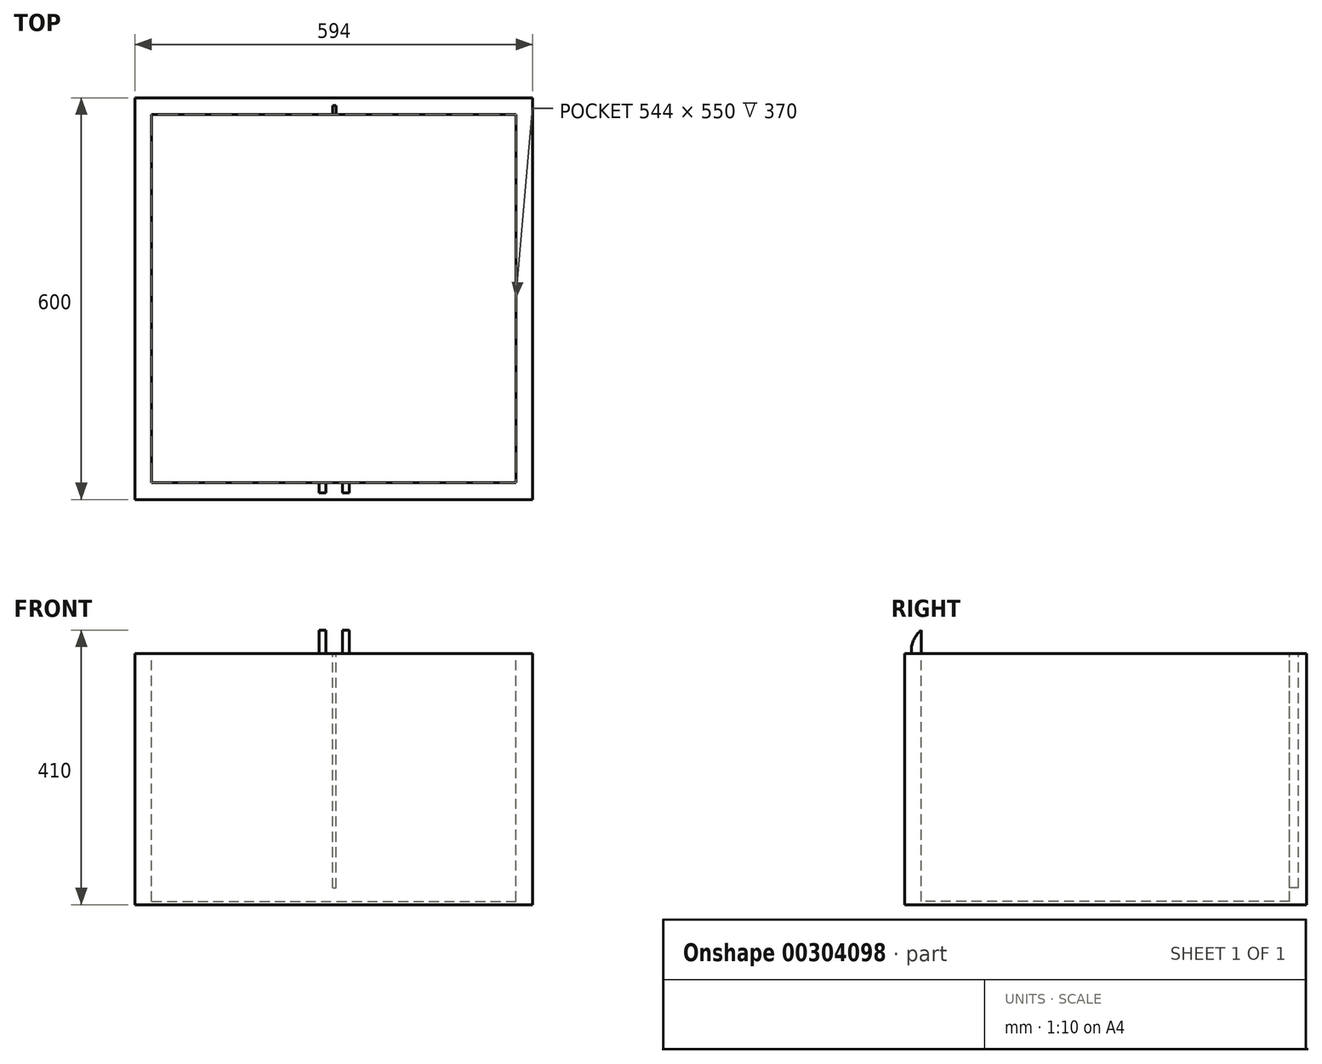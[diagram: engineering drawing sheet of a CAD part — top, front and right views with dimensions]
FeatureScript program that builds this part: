
annotation { "Feature Type Name" : "Feature", "Feature Type Description" : "" }
export const myFeature = defineFeature(function(context is Context, id is Id, definition is map)
    precondition{}
    {
        {
            var Q0;
            Q0=qCreatedBy(makeId("Top.planeOp"),FACE);
            var sketch = newSketch(context, id + "F0", { "sketchPlane" : qUnion([Q0])});
            skLineSegment(sketch, "E0.bottom", {"start": v(-299.36, 336.65) * mm, "end": v(294.64, 336.65) * mm});
            skLineSegment(sketch, "E0.top", {"start": v(-299.36, -263.35) * mm, "end": v(294.64, -263.35) * mm});
            skLineSegment(sketch, "E0.left", {"start": v(-299.36, 336.65) * mm, "end": v(-299.36, -263.35) * mm});
            skLineSegment(sketch, "E0.right", {"start": v(294.64, 336.65) * mm, "end": v(294.64, -263.35) * mm});
            skSolve(sketch);
        }
        {
            var Q0;
            Q0=makeQuery(id+"F0.imprint","IMPRINT",FACE,{"disambiguationData":[TD([[makeQuery(id+"F0.imprint","IMPRINT",EDGE,{"derivedFrom":sQuery(id+"F0.wireOp",EDGE,"E0.bottom")}),-1.0]])]});
            extrude(context, id + "F1", {"entities" : qUnion([Q0]), "depth" : 365 * mm, "offsetDistance" : 25 * mm});
        }
        {
            var Q0;
            Q0=makeQuery(id+"F1.opExtrude","CAP_FACE",FACE,{"disambiguationData":[OSD([sQuery(id+"F0.wireOp",EDGE,"E0.bottom"),sQuery(id+"F0.wireOp",EDGE,"E0.top"),sQuery(id+"F0.wireOp",EDGE,"E0.left"),sQuery(id+"F0.wireOp",EDGE,"E0.right")])],"isStart":false});
            var sketch = newSketch(context, id + "F2", { "sketchPlane" : qUnion([Q0])});
            skLineSegment(sketch, "E1.0", {"start": v(-274.36, 311.65) * mm, "end": v(269.64, 311.65) * mm});
            skLineSegment(sketch, "E1.1", {"start": v(-274.36, 311.65) * mm, "end": v(-274.36, -238.35) * mm});
            skLineSegment(sketch, "E1.2", {"start": v(-274.36, -238.35) * mm, "end": v(269.64, -238.35) * mm});
            skLineSegment(sketch, "E1.3", {"start": v(269.64, 311.65) * mm, "end": v(269.64, -238.35) * mm});
            skSolve(sketch);
        }
        {
            var Q0;
            Q0=makeQuery(id+"F2.imprint","IMPRINT",FACE,{"disambiguationData":[TD([[makeQuery(id+"F2.imprint","IMPRINT",EDGE,{"derivedFrom":sQuery(id+"F2.wireOp",EDGE,"E1.0")}),-1.0]])]});
            extrude(context, id + "F3", {"entities" : qUnion([Q0]), "operationType" : NewBodyOperationType.REMOVE, "oppositeDirection" : true, "depth" : 360 * mm, "offsetDistance" : 25 * mm});
        }
        {
            var Q0;
            Q0=makeQuery(id+"F1.opExtrude","CAP_FACE",FACE,{"disambiguationData":[OSD([sQuery(id+"F0.wireOp",EDGE,"E0.bottom"),sQuery(id+"F0.wireOp",EDGE,"E0.top"),sQuery(id+"F0.wireOp",EDGE,"E0.left"),sQuery(id+"F0.wireOp",EDGE,"E0.right")])],"isStart":false});
            var sketch = newSketch(context, id + "F4", { "sketchPlane" : qUnion([Q0])});
            skLineSegment(sketch, "E2.bottom", {"start": v(-299.36, 336.65) * mm, "end": v(294.64, 336.65) * mm});
            skLineSegment(sketch, "E2.top", {"start": v(-299.36, -263.35) * mm, "end": v(294.64, -263.35) * mm});
            skLineSegment(sketch, "E2.left", {"start": v(-299.36, 336.65) * mm, "end": v(-299.36, -263.35) * mm});
            skLineSegment(sketch, "E2.right", {"start": v(294.64, 336.65) * mm, "end": v(294.64, -263.35) * mm});
            skSolve(sketch);
        }
        {
            var Q0;
            Q0=makeQuery(id+"F4.imprint","IMPRINT",FACE,{"disambiguationData":[TD([[makeQuery(id+"F4.imprint","IMPRINT",EDGE,{"derivedFrom":sQuery(id+"F4.wireOp",EDGE,"E2.bottom")}),-1.0]])]});
            var Q1;
            Q1=makeQuery(id+"F4.imprint","IMPRINT",FACE,{"disambiguationData":[TD([[makeQuery(id+"F4.imprint","IMPRINT",EDGE,{"derivedFrom":makeQuery(id+"F3.boolean.opBoolean","COPY",EDGE,{"derivedFrom":makeQuery(id+"F3.opExtrude","CAP_EDGE",EDGE,{"disambiguationData":[OSD([sQuery(id+"F2.wireOp",EDGE,"E1.0")])],"isStart":true})})}),-1.0]])]});
            extrude(context, id + "F5", {"entities" : qUnion([Q0, Q1]), "operationType" : NewBodyOperationType.ADD, "depth" : 10 * mm, "offsetDistance" : 25 * mm});
        }
        {
            var Q0;
            Q0=makeQuery(id+"F5.opExtrude","CAP_FACE",FACE,{"disambiguationData":[OSD([sQuery(id+"F4.wireOp",EDGE,"E2.bottom"),sQuery(id+"F4.wireOp",EDGE,"E2.top"),sQuery(id+"F4.wireOp",EDGE,"E2.left"),sQuery(id+"F4.wireOp",EDGE,"E2.right")])],"isStart":false});
            var sketch = newSketch(context, id + "F6", { "sketchPlane" : qUnion([Q0])});
            skLineSegment(sketch, "E3.bottom", {"start": v(-249.36, 286.65) * mm, "end": v(-146.86, 286.65) * mm});
            skLineSegment(sketch, "E3.top", {"start": v(-249.36, 140.65) * mm, "end": v(-146.86, 140.65) * mm});
            skLineSegment(sketch, "E3.left", {"start": v(-249.36, 286.65) * mm, "end": v(-249.36, 140.65) * mm});
            skLineSegment(sketch, "E3.right", {"start": v(-146.86, 286.65) * mm, "end": v(-146.86, 140.65) * mm});
            skLineSegment(sketch, "E4.bottom", {"start": v(-131.86, 286.65) * mm, "end": v(-29.36, 286.65) * mm});
            skLineSegment(sketch, "E4.top", {"start": v(-131.86, 140.65) * mm, "end": v(-29.36, 140.65) * mm});
            skLineSegment(sketch, "E4.left", {"start": v(-131.86, 286.65) * mm, "end": v(-131.86, 140.65) * mm});
            skLineSegment(sketch, "E4.right", {"start": v(-29.36, 286.65) * mm, "end": v(-29.36, 140.65) * mm});
            skLineSegment(sketch, "E5.bottom", {"start": v(-249.36, 125.65) * mm, "end": v(-146.86, 125.65) * mm});
            skLineSegment(sketch, "E5.top", {"start": v(-249.36, 50) * mm, "end": v(-146.86, 50) * mm});
            skLineSegment(sketch, "E5.left", {"start": v(-249.36, 125.65) * mm, "end": v(-249.36, 50) * mm});
            skLineSegment(sketch, "E5.right", {"start": v(-146.86, 125.65) * mm, "end": v(-146.86, 50) * mm});
            skLineSegment(sketch, "E6.bottom", {"start": v(-131.86, 125.65) * mm, "end": v(-29.36, 125.65) * mm});
            skLineSegment(sketch, "E6.top", {"start": v(-131.86, 50) * mm, "end": v(-29.36, 50) * mm});
            skLineSegment(sketch, "E6.left", {"start": v(-131.86, 125.65) * mm, "end": v(-131.86, 50) * mm});
            skLineSegment(sketch, "E6.right", {"start": v(-29.36, 125.65) * mm, "end": v(-29.36, 50) * mm});
            skLineSegment(sketch, "E7.bottom", {"start": v(-249.36, 0) * mm, "end": v(-146.86, 0) * mm});
            skLineSegment(sketch, "E7.top", {"start": v(-249.36, -75.65) * mm, "end": v(-146.86, -75.65) * mm});
            skLineSegment(sketch, "E7.left", {"start": v(-249.36, 0) * mm, "end": v(-249.36, -75.65) * mm});
            skLineSegment(sketch, "E7.right", {"start": v(-146.86, 0) * mm, "end": v(-146.86, -75.65) * mm});
            skLineSegment(sketch, "E8.bottom", {"start": v(-131.86, 0) * mm, "end": v(-29.36, 0) * mm});
            skLineSegment(sketch, "E8.top", {"start": v(-131.86, -75.5) * mm, "end": v(-29.36, -75.5) * mm});
            skLineSegment(sketch, "E8.left", {"start": v(-131.86, 0) * mm, "end": v(-131.86, -75.5) * mm});
            skLineSegment(sketch, "E8.right", {"start": v(-29.36, 0) * mm, "end": v(-29.36, -75.5) * mm});
            skLineSegment(sketch, "E9.bottom", {"start": v(-249.36, -90.65) * mm, "end": v(-146.86, -90.65) * mm});
            skLineSegment(sketch, "E9.top", {"start": v(-249.36, -213.35) * mm, "end": v(-146.86, -213.35) * mm});
            skLineSegment(sketch, "E9.left", {"start": v(-249.36, -90.65) * mm, "end": v(-249.36, -213.35) * mm});
            skLineSegment(sketch, "E9.right", {"start": v(-146.86, -90.65) * mm, "end": v(-146.86, -213.35) * mm});
            skLineSegment(sketch, "E10.bottom", {"start": v(-131.86, -90.5) * mm, "end": v(-29.36, -90.5) * mm});
            skLineSegment(sketch, "E10.top", {"start": v(-131.86, -213.35) * mm, "end": v(-29.36, -213.35) * mm});
            skLineSegment(sketch, "E10.left", {"start": v(-131.86, -90.5) * mm, "end": v(-131.86, -213.35) * mm});
            skLineSegment(sketch, "E10.right", {"start": v(-29.36, -90.5) * mm, "end": v(-29.36, -213.35) * mm});
            skLineSegment(sketch, "E11.bottom", {"start": v(0.64, 336.65) * mm, "end": v(-4.36, 336.65) * mm});
            skLineSegment(sketch, "E11.top", {"start": v(0.64, -263.35) * mm, "end": v(-4.36, -263.35) * mm});
            skLineSegment(sketch, "E11.left", {"start": v(0.64, 336.65) * mm, "end": v(0.64, -263.35) * mm});
            skLineSegment(sketch, "E11.right", {"start": v(-4.36, 336.65) * mm, "end": v(-4.36, -263.35) * mm});
            skLineSegment(sketch, "E12.bottom", {"start": v(25.64, 287.34) * mm, "end": v(127.64, 287.34) * mm});
            skLineSegment(sketch, "E12.top", {"start": v(25.64, 141.34) * mm, "end": v(127.64, 141.34) * mm});
            skLineSegment(sketch, "E12.left", {"start": v(25.64, 287.34) * mm, "end": v(25.64, 141.34) * mm});
            skLineSegment(sketch, "E12.right", {"start": v(127.64, 287.34) * mm, "end": v(127.64, 141.34) * mm});
            skLineSegment(sketch, "E13.bottom", {"start": v(142.64, 286.65) * mm, "end": v(244.64, 286.65) * mm});
            skLineSegment(sketch, "E13.top", {"start": v(142.64, 140.65) * mm, "end": v(244.64, 140.65) * mm});
            skLineSegment(sketch, "E13.left", {"start": v(142.64, 286.65) * mm, "end": v(142.64, 140.65) * mm});
            skLineSegment(sketch, "E13.right", {"start": v(244.64, 286.65) * mm, "end": v(244.64, 140.65) * mm});
            skLineSegment(sketch, "E14.bottom", {"start": v(25.64, 126.34) * mm, "end": v(127.64, 126.34) * mm});
            skLineSegment(sketch, "E14.top", {"start": v(25.64, 50.68) * mm, "end": v(127.64, 50.68) * mm});
            skLineSegment(sketch, "E14.left", {"start": v(25.64, 126.34) * mm, "end": v(25.64, 50.68) * mm});
            skLineSegment(sketch, "E14.right", {"start": v(127.64, 126.34) * mm, "end": v(127.64, 50.68) * mm});
            skLineSegment(sketch, "E15.bottom", {"start": v(142.64, 125.65) * mm, "end": v(244.64, 125.65) * mm});
            skLineSegment(sketch, "E15.top", {"start": v(142.64, 50.68) * mm, "end": v(244.64, 50.68) * mm});
            skLineSegment(sketch, "E15.left", {"start": v(142.64, 125.65) * mm, "end": v(142.64, 50.68) * mm});
            skLineSegment(sketch, "E15.right", {"start": v(244.64, 125.65) * mm, "end": v(244.64, 50.68) * mm});
            skLineSegment(sketch, "E16.bottom", {"start": v(25.64, 0.68) * mm, "end": v(127.64, 0.68) * mm});
            skLineSegment(sketch, "E16.top", {"start": v(25.64, -74.97) * mm, "end": v(127.64, -74.97) * mm});
            skLineSegment(sketch, "E16.left", {"start": v(25.64, 0.68) * mm, "end": v(25.64, -74.97) * mm});
            skLineSegment(sketch, "E16.right", {"start": v(127.64, 0.68) * mm, "end": v(127.64, -74.97) * mm});
            skLineSegment(sketch, "E17.bottom", {"start": v(142.64, 0.68) * mm, "end": v(244.64, 0.68) * mm});
            skLineSegment(sketch, "E17.top", {"start": v(142.64, -74.82) * mm, "end": v(244.64, -74.82) * mm});
            skLineSegment(sketch, "E17.left", {"start": v(142.64, 0.68) * mm, "end": v(142.64, -74.82) * mm});
            skLineSegment(sketch, "E17.right", {"start": v(244.64, 0.68) * mm, "end": v(244.64, -74.82) * mm});
            skLineSegment(sketch, "E18.bottom", {"start": v(25.64, -89.97) * mm, "end": v(127.64, -89.97) * mm});
            skLineSegment(sketch, "E18.top", {"start": v(25.64, -213.35) * mm, "end": v(127.64, -213.35) * mm});
            skLineSegment(sketch, "E18.left", {"start": v(25.64, -89.97) * mm, "end": v(25.64, -213.35) * mm});
            skLineSegment(sketch, "E18.right", {"start": v(127.64, -89.97) * mm, "end": v(127.64, -213.35) * mm});
            skLineSegment(sketch, "E19.bottom", {"start": v(142.64, -89.82) * mm, "end": v(244.64, -89.82) * mm});
            skLineSegment(sketch, "E19.top", {"start": v(142.64, -213.35) * mm, "end": v(244.64, -213.35) * mm});
            skLineSegment(sketch, "E19.left", {"start": v(142.64, -89.82) * mm, "end": v(142.64, -213.35) * mm});
            skLineSegment(sketch, "E19.right", {"start": v(244.64, -89.82) * mm, "end": v(244.64, -213.35) * mm});
            skLineSegment(sketch, "E20", {"start": v(-4.36, 324.98) * mm, "end": v(0.64, 324.98) * mm});
            skLineSegment(sketch, "E21", {"start": v(-4.36, -249.89) * mm, "end": v(0, -249.89) * mm});
            skLineSegment(sketch, "E22", {"start": v(0, -249.89) * mm, "end": v(0.64, -249.89) * mm});
            skSolve(sketch);
        }
        {
            var Q0;
            Q0=makeQuery(id+"F6.imprint","IMPRINT",FACE,{"disambiguationData":[TD([[makeQuery(id+"F6.imprint","IMPRINT",EDGE,{"derivedFrom":sQuery(id+"F6.wireOp",EDGE,"E3.bottom")}),-1.0]])]});
            var Q1;
            Q1=makeQuery(id+"F6.imprint","IMPRINT",FACE,{"disambiguationData":[TD([[makeQuery(id+"F6.imprint","IMPRINT",EDGE,{"derivedFrom":sQuery(id+"F6.wireOp",EDGE,"E4.bottom")}),-1.0]])]});
            var Q2;
            Q2=makeQuery(id+"F6.imprint","IMPRINT",FACE,{"disambiguationData":[TD([[makeQuery(id+"F6.imprint","IMPRINT",EDGE,{"derivedFrom":sQuery(id+"F6.wireOp",EDGE,"E6.bottom")}),-1.0]])]});
            var Q3;
            Q3=makeQuery(id+"F6.imprint","IMPRINT",FACE,{"disambiguationData":[TD([[makeQuery(id+"F6.imprint","IMPRINT",EDGE,{"derivedFrom":sQuery(id+"F6.wireOp",EDGE,"E5.bottom")}),-1.0]])]});
            var Q4;
            Q4=makeQuery(id+"F6.imprint","IMPRINT",FACE,{"disambiguationData":[TD([[makeQuery(id+"F6.imprint","IMPRINT",EDGE,{"derivedFrom":sQuery(id+"F6.wireOp",EDGE,"E12.bottom")}),-1.0]])]});
            var Q5;
            Q5=makeQuery(id+"F6.imprint","IMPRINT",FACE,{"disambiguationData":[TD([[makeQuery(id+"F6.imprint","IMPRINT",EDGE,{"derivedFrom":sQuery(id+"F6.wireOp",EDGE,"E13.bottom")}),-1.0]])]});
            var Q6;
            Q6=makeQuery(id+"F6.imprint","IMPRINT",FACE,{"disambiguationData":[TD([[makeQuery(id+"F6.imprint","IMPRINT",EDGE,{"derivedFrom":sQuery(id+"F6.wireOp",EDGE,"E15.bottom")}),-1.0]])]});
            var Q7;
            Q7=makeQuery(id+"F6.imprint","IMPRINT",FACE,{"disambiguationData":[TD([[makeQuery(id+"F6.imprint","IMPRINT",EDGE,{"derivedFrom":sQuery(id+"F6.wireOp",EDGE,"E14.bottom")}),-1.0]])]});
            var Q8;
            Q8=makeQuery(id+"F6.imprint","IMPRINT",FACE,{"disambiguationData":[TD([[makeQuery(id+"F6.imprint","IMPRINT",EDGE,{"derivedFrom":sQuery(id+"F6.wireOp",EDGE,"E16.bottom")}),-1.0]])]});
            var Q9;
            Q9=makeQuery(id+"F6.imprint","IMPRINT",FACE,{"disambiguationData":[TD([[makeQuery(id+"F6.imprint","IMPRINT",EDGE,{"derivedFrom":sQuery(id+"F6.wireOp",EDGE,"E17.bottom")}),-1.0]])]});
            var Q10;
            Q10=makeQuery(id+"F6.imprint","IMPRINT",FACE,{"disambiguationData":[TD([[makeQuery(id+"F6.imprint","IMPRINT",EDGE,{"derivedFrom":sQuery(id+"F6.wireOp",EDGE,"E19.bottom")}),-1.0]])]});
            var Q11;
            Q11=makeQuery(id+"F6.imprint","IMPRINT",FACE,{"disambiguationData":[TD([[makeQuery(id+"F6.imprint","IMPRINT",EDGE,{"derivedFrom":sQuery(id+"F6.wireOp",EDGE,"E18.bottom")}),-1.0]])]});
            var Q12;
            Q12=makeQuery(id+"F6.imprint","IMPRINT",FACE,{"disambiguationData":[TD([[makeQuery(id+"F6.imprint","IMPRINT",EDGE,{"derivedFrom":sQuery(id+"F6.wireOp",EDGE,"E10.bottom")}),-1.0]])]});
            var Q13;
            Q13=makeQuery(id+"F6.imprint","IMPRINT",FACE,{"disambiguationData":[TD([[makeQuery(id+"F6.imprint","IMPRINT",EDGE,{"derivedFrom":sQuery(id+"F6.wireOp",EDGE,"E8.bottom")}),-1.0]])]});
            var Q14;
            Q14=makeQuery(id+"F6.imprint","IMPRINT",FACE,{"disambiguationData":[TD([[makeQuery(id+"F6.imprint","IMPRINT",EDGE,{"derivedFrom":sQuery(id+"F6.wireOp",EDGE,"E7.bottom")}),-1.0]])]});
            var Q15;
            Q15=makeQuery(id+"F6.imprint","IMPRINT",FACE,{"disambiguationData":[TD([[makeQuery(id+"F6.imprint","IMPRINT",EDGE,{"derivedFrom":sQuery(id+"F6.wireOp",EDGE,"E9.bottom")}),-1.0]])]});
            var Q16;
            {var subQ0=sQuery(id+"F6.wireOp",EDGE,"E20");Q16=makeQuery(id+"F6.imprint","IMPRINT",FACE,{"disambiguationData":[TD([[makeQuery(id+"F6.imprint","IMPRINT",EDGE,{"derivedFrom":subQ0}),-1.0]])]});}
            extrude(context, id + "F7", {"entities" : qUnion([Q0, Q1, Q2, Q3, Q4, Q5, Q6, Q7, Q8, Q9, Q10, Q11, Q12, Q13, Q14, Q15, Q16]), "operationType" : NewBodyOperationType.REMOVE, "oppositeDirection" : true, "depth" : 350 * mm, "offsetDistance" : 25 * mm});
        }
        {
            var Q0;
            Q0=makeQuery(id+"F5.opExtrude","CAP_FACE",FACE,{"disambiguationData":[OSD([sQuery(id+"F4.wireOp",EDGE,"E2.bottom"),sQuery(id+"F4.wireOp",EDGE,"E2.top"),sQuery(id+"F4.wireOp",EDGE,"E2.left"),sQuery(id+"F4.wireOp",EDGE,"E2.right")])],"isStart":false});
            var sketch = newSketch(context, id + "F8", { "sketchPlane" : qUnion([Q0])});
            skLineSegment(sketch, "E23.bottom", {"start": v(-14.36, -253.35) * mm, "end": v(-24.36, -253.35) * mm});
            skLineSegment(sketch, "E23.top", {"start": v(-14.36, -163.35) * mm, "end": v(-24.36, -163.35) * mm});
            skLineSegment(sketch, "E23.left", {"start": v(-14.36, -253.35) * mm, "end": v(-14.36, -163.35) * mm});
            skLineSegment(sketch, "E23.right", {"start": v(-24.36, -253.35) * mm, "end": v(-24.36, -163.35) * mm});
            skLineSegment(sketch, "E24.bottom", {"start": v(20.64, -253.35) * mm, "end": v(10.64, -253.35) * mm});
            skLineSegment(sketch, "E24.top", {"start": v(20.64, -163.35) * mm, "end": v(10.64, -163.35) * mm});
            skLineSegment(sketch, "E24.left", {"start": v(20.64, -253.35) * mm, "end": v(20.64, -163.35) * mm});
            skLineSegment(sketch, "E24.right", {"start": v(10.64, -253.35) * mm, "end": v(10.64, -163.35) * mm});
            skSolve(sketch);
        }
        {
            var Q0;
            Q0=makeQuery(id+"F8.imprint","IMPRINT",FACE,{"disambiguationData":[TD([[makeQuery(id+"F8.imprint","IMPRINT",EDGE,{"derivedFrom":sQuery(id+"F8.wireOp",EDGE,"E23.bottom")}),-1.0]])]});
            var Q1;
            Q1=makeQuery(id+"F8.imprint","IMPRINT",FACE,{"disambiguationData":[TD([[makeQuery(id+"F8.imprint","IMPRINT",EDGE,{"derivedFrom":sQuery(id+"F8.wireOp",EDGE,"E24.bottom")}),-1.0]])]});
            extrude(context, id + "F9", {"entities" : qUnion([Q0, Q1]), "depth" : 35 * mm, "offsetDistance" : 25 * mm});
        }
        {
            var Q0;
            Q0=makeQuery(id+"F9.opExtrude","CAP_EDGE",EDGE,{"disambiguationData":[OSD([sQuery(id+"F8.wireOp",EDGE,"E24.top")])],"isStart":false});
            var Q1;
            Q1=makeQuery(id+"F9.opExtrude","CAP_EDGE",EDGE,{"disambiguationData":[OSD([sQuery(id+"F8.wireOp",EDGE,"E23.top")])],"isStart":false});
            var Q2;
            Q2=makeQuery(id+"F9.opExtrude","CAP_EDGE",EDGE,{"disambiguationData":[OSD([sQuery(id+"F8.wireOp",EDGE,"E23.bottom")])],"isStart":false});
            var Q3;
            Q3=makeQuery(id+"F9.opExtrude","CAP_EDGE",EDGE,{"disambiguationData":[OSD([sQuery(id+"F8.wireOp",EDGE,"E24.bottom")])],"isStart":false});
            fillet(context, id + "F10", {"entities" : qUnion([Q0, Q1, Q2, Q3]), "radius" : 40 * mm, "tangentPropagation" : true, "allowEdgeOverflow" : false});
        }
        {
            var Q0;
            Q0=makeQuery(id+"F9.opExtrude","SWEPT_FACE",FACE,{"disambiguationData":[OSD([sQuery(id+"F8.wireOp",EDGE,"E23.right")])]});
            var sketch = newSketch(context, id + "F11", { "sketchPlane" : qUnion([Q0])});
            skLineSegment(sketch, "E25.0", {"start": v(213.66, 402) * mm, "end": v(203.03, 402) * mm});
            skArc(sketch, "E25.1", {"start": v(242.9, 383) * mm, "mid": v(231.1, 396.83) * mm, "end": v(213.66, 402) * mm});
            skLineSegment(sketch, "E25.2", {"start": v(173.8, 383) * mm, "end": v(242.9, 383) * mm});
            skArc(sketch, "E25.3", {"start": v(203.03, 402) * mm, "mid": v(185.6, 396.83) * mm, "end": v(173.8, 383) * mm});
            skSolve(sketch);
        }
        {
            var Q0;
            Q0=makeQuery(id+"F11.imprint","IMPRINT",FACE,{"disambiguationData":[TD([[makeQuery(id+"F11.imprint","IMPRINT",EDGE,{"derivedFrom":sQuery(id+"F11.wireOp",EDGE,"E25.0")}),1.0]])]});
            extrude(context, id + "F12", {"entities" : qUnion([Q0]), "operationType" : NewBodyOperationType.REMOVE, "oppositeDirection" : true, "depth" : 100 * mm, "offsetDistance" : 25 * mm});
        }
    });
